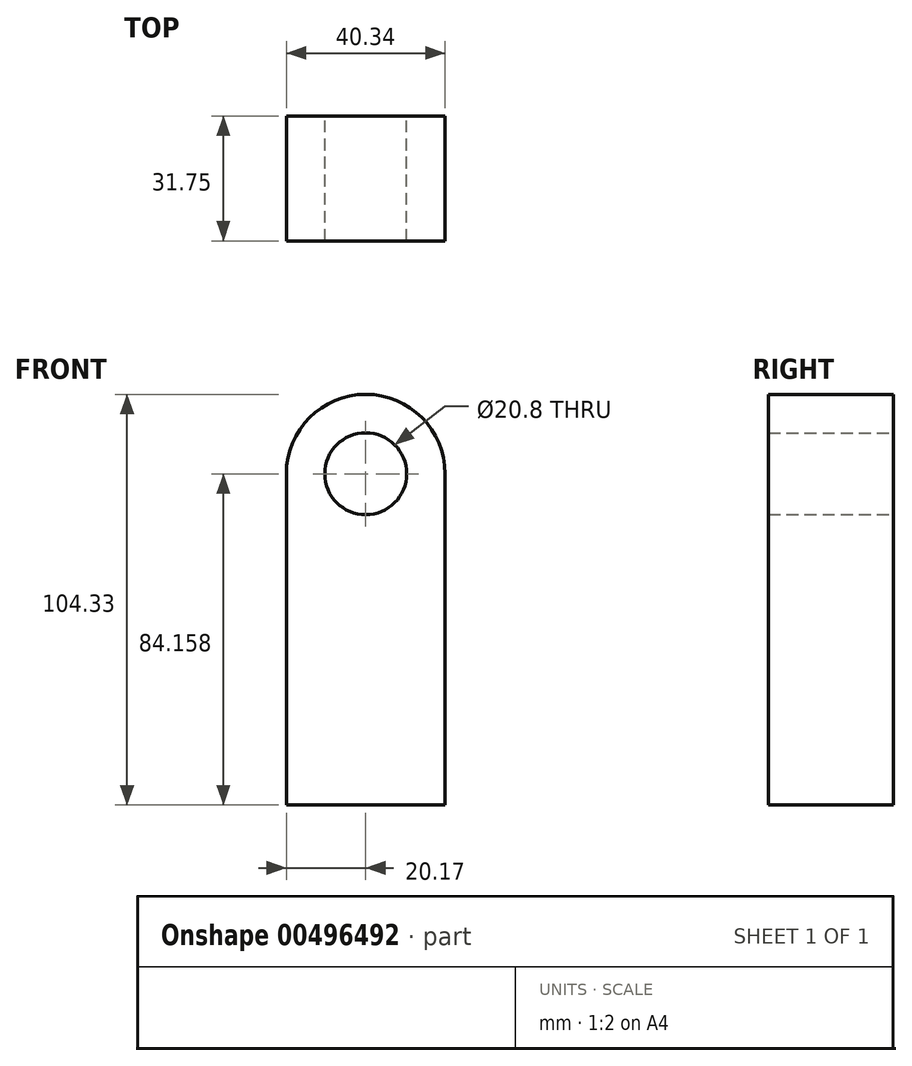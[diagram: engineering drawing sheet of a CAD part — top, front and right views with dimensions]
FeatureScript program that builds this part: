
annotation { "Feature Type Name" : "Feature", "Feature Type Description" : "" }
export const myFeature = defineFeature(function(context is Context, id is Id, definition is map)
    precondition{}
    {
        {
            var Q0;
            Q0=qCreatedBy(makeId("Front.planeOp"),FACE);
            var sketch = newSketch(context, id + "F0", { "sketchPlane" : qUnion([Q0])});
            skLineSegment(sketch, "E0.top", {"start": v(20.17, -42.08) * mm, "end": v(-20.17, -42.08) * mm});
            skLineSegment(sketch, "E0.left", {"start": v(20.17, 42.08) * mm, "end": v(20.17, -42.08) * mm});
            skLineSegment(sketch, "E0.right", {"start": v(-20.17, 42.08) * mm, "end": v(-20.17, -42.08) * mm});
            skPoint(sketch, "E0.middle", {"position": v(0, 0) * mm});
            skArc(sketch, "E1", {"start": v(20.17, 42.08) * mm, "mid": v(0, 62.25) * mm, "end": v(-20.17, 42.08) * mm});
            skCircle(sketch, "E2", {"center": v(0, 42.08) * mm, "radius": 10.4 * mm});
            skSolve(sketch);
        }
        {
            var Q0;
            Q0=makeQuery(id+"F0.imprint","IMPRINT",FACE,{"disambiguationData":[TD([[makeQuery(id+"F0.imprint","IMPRINT",EDGE,{"derivedFrom":sQuery(id+"F0.wireOp",EDGE,"E0.top")}),-1.0]])]});
            extrude(context, id + "F1", {"entities" : qUnion([Q0]), "depth" : 31.75 * mm});
        }
    });
